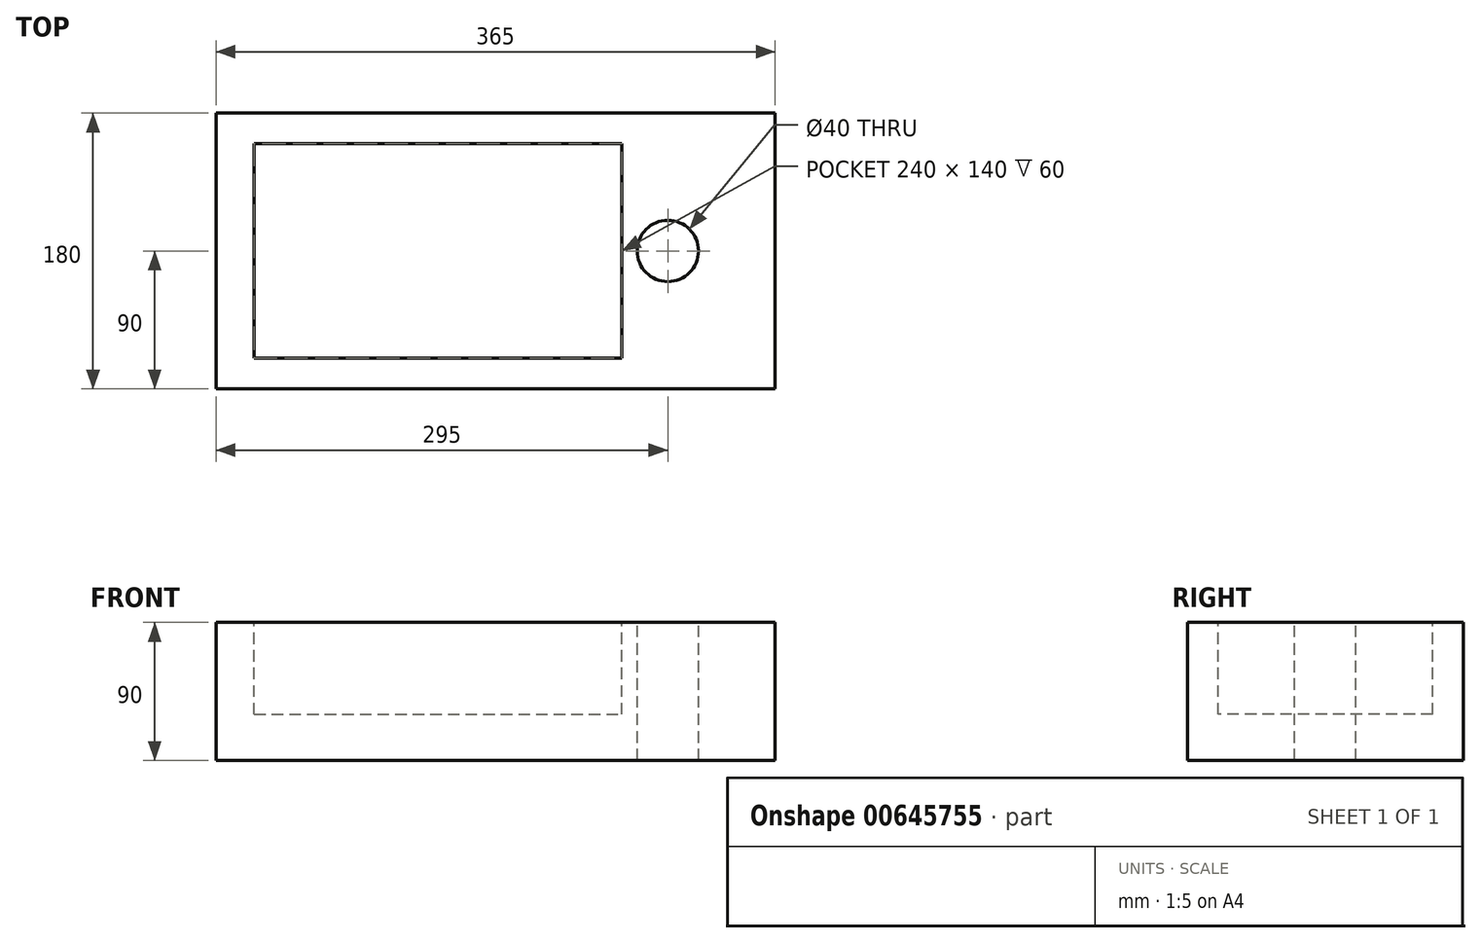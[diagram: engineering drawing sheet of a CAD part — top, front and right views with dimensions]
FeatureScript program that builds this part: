
annotation { "Feature Type Name" : "Feature", "Feature Type Description" : "" }
export const myFeature = defineFeature(function(context is Context, id is Id, definition is map)
    precondition{}
    {
        {
            var Q0;
            Q0=qCreatedBy(makeId("Top.planeOp"),FACE);
            var sketch = newSketch(context, id + "F0", { "sketchPlane" : qUnion([Q0])});
            skLineSegment(sketch, "E0.bottom", {"start": v(0, 0) * mm, "end": v(365, 0) * mm});
            skLineSegment(sketch, "E0.top", {"start": v(0, 180) * mm, "end": v(365, 180) * mm});
            skLineSegment(sketch, "E0.left", {"start": v(0, 0) * mm, "end": v(0, 180) * mm});
            skLineSegment(sketch, "E0.right", {"start": v(365, 0) * mm, "end": v(365, 180) * mm});
            skSolve(sketch);
        }
        {
            var Q0;
            Q0=qSketchRegion(id+"F0",true);
            extrude(context, id + "F1", {"entities" : qUnion([Q0]), "depth" : 90 * mm});
        }
        {
            var Q0;
            Q0=makeQuery(id+"F1.opExtrude","CAP_FACE",FACE,{"disambiguationData":[OSD([sQuery(id+"F0.wireOp",EDGE,"E0.bottom"),sQuery(id+"F0.wireOp",EDGE,"E0.top"),sQuery(id+"F0.wireOp",EDGE,"E0.left"),sQuery(id+"F0.wireOp",EDGE,"E0.right")])],"isStart":false});
            var sketch = newSketch(context, id + "F2", { "sketchPlane" : qUnion([Q0])});
            skLineSegment(sketch, "E1.bottom", {"start": v(25, 160) * mm, "end": v(265, 160) * mm});
            skLineSegment(sketch, "E1.top", {"start": v(25, 20) * mm, "end": v(265, 20) * mm});
            skLineSegment(sketch, "E1.left", {"start": v(25, 160) * mm, "end": v(25, 20) * mm});
            skLineSegment(sketch, "E1.right", {"start": v(265, 160) * mm, "end": v(265, 20) * mm});
            skLineSegment(sketch, "E2", {"start": v(0, 90) * mm, "end": v(268.68, 90) * mm, "construction": true});
            skSolve(sketch);
        }
        {
            var Q0;
            Q0=qSketchRegion(id+"F2",true);
            extrude(context, id + "F3", {"entities" : qUnion([Q0]), "operationType" : NewBodyOperationType.REMOVE, "oppositeDirection" : true, "depth" : 60 * mm});
        }
        {
            var Q0;
            Q0=makeQuery(id+"F1.opExtrude","CAP_FACE",FACE,{"disambiguationData":[OSD([sQuery(id+"F0.wireOp",EDGE,"E0.bottom"),sQuery(id+"F0.wireOp",EDGE,"E0.top"),sQuery(id+"F0.wireOp",EDGE,"E0.left"),sQuery(id+"F0.wireOp",EDGE,"E0.right")])],"isStart":false});
            var sketch = newSketch(context, id + "F4", { "sketchPlane" : qUnion([Q0])});
            skLineSegment(sketch, "E3", {"start": v(265, 90) * mm, "end": v(344.24, 90) * mm, "construction": true});
            skCircle(sketch, "E4", {"center": v(295, 90) * mm, "radius": 20 * mm});
            skSolve(sketch);
        }
        {
            var Q0;
            Q0=qSketchRegion(id+"F4",true);
            extrude(context, id + "F5", {"entities" : qUnion([Q0]), "operationType" : NewBodyOperationType.REMOVE, "endBound" : BoundingType.THROUGH_ALL, "oppositeDirection" : true, "depth" : 25 * mm});
        }
    });
